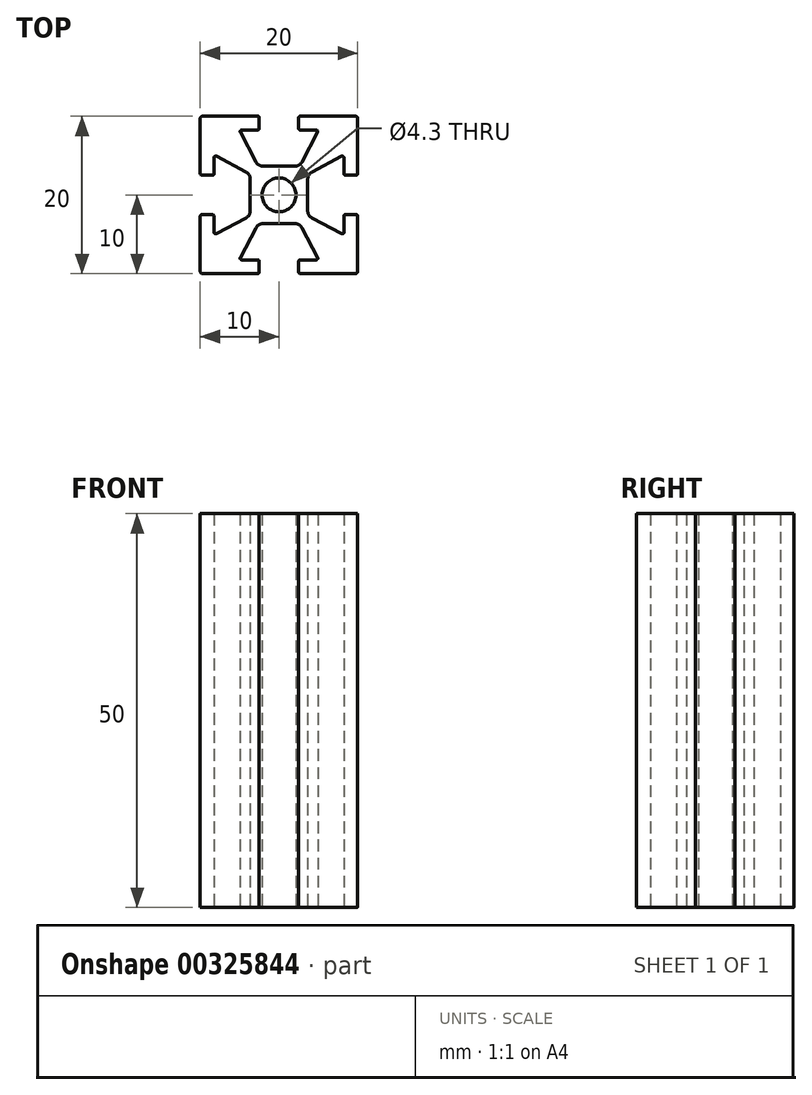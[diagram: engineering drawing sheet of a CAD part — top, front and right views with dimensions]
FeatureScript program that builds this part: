
annotation { "Feature Type Name" : "Feature", "Feature Type Description" : "" }
export const myFeature = defineFeature(function(context is Context, id is Id, definition is map)
    precondition{}
    {
        {
            var Q0;
            Q0=qCreatedBy(makeId("Top.planeOp"),FACE);
            var sketch = newSketch(context, id + "F0", { "sketchPlane" : qUnion([Q0])});
            skLineSegment(sketch, "E0", {"start": v(-9.7, 10) * mm, "end": v(-2.7, 10) * mm});
            skLineSegment(sketch, "E1", {"start": v(-2.5, 9.8) * mm, "end": v(-2.5, 8.45) * mm});
            skLineSegment(sketch, "E2", {"start": v(-2.7, 8.25) * mm, "end": v(-4.73, 8.25) * mm});
            skLineSegment(sketch, "E3", {"start": v(-4.9, 7.96) * mm, "end": v(-2.92, 4.18) * mm});
            skLineSegment(sketch, "E4", {"start": v(-2.03, 3.65) * mm, "end": v(0, 3.65) * mm});
            skLineSegment(sketch, "E5", {"start": v(0, 0) * mm, "end": v(-15.4, 15.4) * mm, "construction": true});
            skPoint(sketch, "E6.visualSharp", {"position": v(-5.06, 8.25) * mm});
            skArc(sketch, "E6.filletArc", {"start": v(-4.73, 8.25) * mm, "mid": v(-4.9, 8.15) * mm, "end": v(-4.9, 7.96) * mm});
            skPoint(sketch, "E7.visualSharp", {"position": v(-2.64, 3.65) * mm});
            skArc(sketch, "E7.filletArc", {"start": v(-2.92, 4.18) * mm, "mid": v(-2.55, 3.8) * mm, "end": v(-2.03, 3.65) * mm});
            skPoint(sketch, "E8.visualSharp", {"position": v(-2.5, 8.25) * mm});
            skArc(sketch, "E8.filletArc", {"start": v(-2.7, 8.25) * mm, "mid": v(-2.56, 8.3) * mm, "end": v(-2.5, 8.45) * mm});
            skPoint(sketch, "E9.visualSharp", {"position": v(-2.5, 10) * mm});
            skArc(sketch, "E9.filletArc", {"start": v(-2.5, 9.8) * mm, "mid": v(-2.56, 9.94) * mm, "end": v(-2.7, 10) * mm});
            skArc(sketch, "E10.MirrorCS", {"start": v(-8.25, 2.7) * mm, "mid": v(-8.3, 2.56) * mm, "end": v(-8.45, 2.5) * mm});
            skArc(sketch, "E11.MirrorCS", {"start": v(-4.18, 2.92) * mm, "mid": v(-3.8, 2.55) * mm, "end": v(-3.65, 2.03) * mm});
            skArc(sketch, "E12.MirrorCS", {"start": v(-9.8, 2.5) * mm, "mid": v(-9.94, 2.56) * mm, "end": v(-10, 2.7) * mm});
            skArc(sketch, "E13.MirrorCS", {"start": v(-8.25, 4.73) * mm, "mid": v(-8.15, 4.9) * mm, "end": v(-7.96, 4.9) * mm});
            skLineSegment(sketch, "E14.MirrorCS", {"start": v(-8.25, 2.7) * mm, "end": v(-8.25, 4.73) * mm});
            skLineSegment(sketch, "E15.MirrorCS", {"start": v(-9.8, 2.5) * mm, "end": v(-8.45, 2.5) * mm});
            skPoint(sketch, "E16.MirrorP", {"position": v(-10, 2.5) * mm});
            skPoint(sketch, "E17.MirrorP", {"position": v(-8.25, 5.06) * mm});
            skLineSegment(sketch, "E18.MirrorCS", {"start": v(-7.96, 4.9) * mm, "end": v(-4.18, 2.92) * mm});
            skPoint(sketch, "E19.MirrorP", {"position": v(-3.65, 2.64) * mm});
            skPoint(sketch, "E20.MirrorP", {"position": v(-8.25, 2.5) * mm});
            skLineSegment(sketch, "E21.MirrorCS", {"start": v(-10, 9.7) * mm, "end": v(-10, 2.7) * mm});
            skLineSegment(sketch, "E22.MirrorCS", {"start": v(-3.65, 2.03) * mm, "end": v(-3.65, 0) * mm});
            skPoint(sketch, "E23.visualSharp", {"position": v(-10, 10) * mm});
            skArc(sketch, "E23.filletArc", {"start": v(-9.7, 10) * mm, "mid": v(-9.91, 9.91) * mm, "end": v(-10, 9.7) * mm});
            skArc(sketch, "E24.MirrorCS", {"start": v(2.92, 4.18) * mm, "mid": v(2.55, 3.8) * mm, "end": v(2.03, 3.65) * mm});
            skArc(sketch, "E25.MirrorCS", {"start": v(4.18, 2.92) * mm, "mid": v(3.8, 2.55) * mm, "end": v(3.65, 2.03) * mm});
            skArc(sketch, "E26.MirrorCS", {"start": v(2.7, 8.25) * mm, "mid": v(2.56, 8.3) * mm, "end": v(2.5, 8.45) * mm});
            skArc(sketch, "E27.MirrorCS", {"start": v(8.25, 2.7) * mm, "mid": v(8.3, 2.56) * mm, "end": v(8.45, 2.5) * mm});
            skArc(sketch, "E28.MirrorCS", {"start": v(4.73, 8.25) * mm, "mid": v(4.9, 8.15) * mm, "end": v(4.9, 7.96) * mm});
            skArc(sketch, "E29.MirrorCS", {"start": v(9.7, 10) * mm, "mid": v(9.91, 9.91) * mm, "end": v(10, 9.7) * mm});
            skArc(sketch, "E30.MirrorCS", {"start": v(2.5, 9.8) * mm, "mid": v(2.56, 9.94) * mm, "end": v(2.7, 10) * mm});
            skArc(sketch, "E31.MirrorCS", {"start": v(9.8, 2.5) * mm, "mid": v(9.94, 2.56) * mm, "end": v(10, 2.7) * mm});
            skArc(sketch, "E32.MirrorCS", {"start": v(8.25, 4.73) * mm, "mid": v(8.15, 4.9) * mm, "end": v(7.96, 4.9) * mm});
            skLineSegment(sketch, "E33.MirrorCS", {"start": v(2.03, 3.65) * mm, "end": v(0, 3.65) * mm});
            skPoint(sketch, "E34.MirrorP", {"position": v(2.64, 3.65) * mm});
            skLineSegment(sketch, "E35.MirrorCS", {"start": v(3.65, 2.03) * mm, "end": v(3.65, 0) * mm});
            skLineSegment(sketch, "E36.MirrorCS", {"start": v(2.5, 9.8) * mm, "end": v(2.5, 8.45) * mm});
            skLineSegment(sketch, "E37.MirrorCS", {"start": v(8.25, 2.7) * mm, "end": v(8.25, 4.73) * mm});
            skPoint(sketch, "E38.MirrorP", {"position": v(8.25, 5.06) * mm});
            skLineSegment(sketch, "E39.MirrorCS", {"start": v(4.9, 7.96) * mm, "end": v(2.92, 4.18) * mm});
            skLineSegment(sketch, "E40.MirrorCS", {"start": v(7.96, 4.9) * mm, "end": v(4.18, 2.92) * mm});
            skPoint(sketch, "E41.MirrorP", {"position": v(8.25, 2.5) * mm});
            skPoint(sketch, "E42.MirrorP", {"position": v(5.06, 8.25) * mm});
            skPoint(sketch, "E43.MirrorP", {"position": v(10, 10) * mm});
            skPoint(sketch, "E44.MirrorP", {"position": v(10, 2.5) * mm});
            skLineSegment(sketch, "E45.MirrorCS", {"start": v(9.7, 10) * mm, "end": v(2.7, 10) * mm});
            skLineSegment(sketch, "E46.MirrorCS", {"start": v(9.8, 2.5) * mm, "end": v(8.45, 2.5) * mm});
            skPoint(sketch, "E47.MirrorP", {"position": v(2.5, 8.25) * mm});
            skPoint(sketch, "E48.MirrorP", {"position": v(2.5, 10) * mm});
            skLineSegment(sketch, "E49.MirrorCS", {"start": v(10, 9.7) * mm, "end": v(10, 2.7) * mm});
            skLineSegment(sketch, "E50.MirrorCS", {"start": v(2.7, 8.25) * mm, "end": v(4.73, 8.25) * mm});
            skPoint(sketch, "E51.MirrorP", {"position": v(3.65, 2.64) * mm});
            skArc(sketch, "E52.MirrorCS", {"start": v(-9.7, -10) * mm, "mid": v(-9.91, -9.91) * mm, "end": v(-10, -9.7) * mm});
            skArc(sketch, "E53.MirrorCS", {"start": v(-2.92, -4.18) * mm, "mid": v(-2.55, -3.8) * mm, "end": v(-2.03, -3.65) * mm});
            skArc(sketch, "E54.MirrorCS", {"start": v(-4.18, -2.92) * mm, "mid": v(-3.8, -2.55) * mm, "end": v(-3.65, -2.03) * mm});
            skArc(sketch, "E55.MirrorCS", {"start": v(2.92, -4.18) * mm, "mid": v(2.55, -3.8) * mm, "end": v(2.03, -3.65) * mm});
            skArc(sketch, "E56.MirrorCS", {"start": v(4.18, -2.92) * mm, "mid": v(3.8, -2.55) * mm, "end": v(3.65, -2.03) * mm});
            skArc(sketch, "E57.MirrorCS", {"start": v(2.7, -8.25) * mm, "mid": v(2.56, -8.3) * mm, "end": v(2.5, -8.45) * mm});
            skArc(sketch, "E58.MirrorCS", {"start": v(9.7, -10) * mm, "mid": v(9.91, -9.91) * mm, "end": v(10, -9.7) * mm});
            skArc(sketch, "E59.MirrorCS", {"start": v(-4.73, -8.25) * mm, "mid": v(-4.9, -8.15) * mm, "end": v(-4.9, -7.96) * mm});
            skArc(sketch, "E60.MirrorCS", {"start": v(8.25, -2.7) * mm, "mid": v(8.3, -2.56) * mm, "end": v(8.45, -2.5) * mm});
            skArc(sketch, "E61.MirrorCS", {"start": v(2.5, -9.8) * mm, "mid": v(2.56, -9.94) * mm, "end": v(2.7, -10) * mm});
            skArc(sketch, "E62.MirrorCS", {"start": v(-9.8, -2.5) * mm, "mid": v(-9.94, -2.56) * mm, "end": v(-10, -2.7) * mm});
            skArc(sketch, "E63.MirrorCS", {"start": v(-8.25, -4.73) * mm, "mid": v(-8.15, -4.9) * mm, "end": v(-7.96, -4.9) * mm});
            skArc(sketch, "E64.MirrorCS", {"start": v(-2.7, -8.25) * mm, "mid": v(-2.56, -8.3) * mm, "end": v(-2.5, -8.45) * mm});
            skArc(sketch, "E65.MirrorCS", {"start": v(8.25, -4.73) * mm, "mid": v(8.15, -4.9) * mm, "end": v(7.96, -4.9) * mm});
            skArc(sketch, "E66.MirrorCS", {"start": v(4.73, -8.25) * mm, "mid": v(4.9, -8.15) * mm, "end": v(4.9, -7.96) * mm});
            skArc(sketch, "E67.MirrorCS", {"start": v(-8.25, -2.7) * mm, "mid": v(-8.3, -2.56) * mm, "end": v(-8.45, -2.5) * mm});
            skArc(sketch, "E68.MirrorCS", {"start": v(-2.5, -9.8) * mm, "mid": v(-2.56, -9.94) * mm, "end": v(-2.7, -10) * mm});
            skArc(sketch, "E69.MirrorCS", {"start": v(9.8, -2.5) * mm, "mid": v(9.94, -2.56) * mm, "end": v(10, -2.7) * mm});
            skLineSegment(sketch, "E70.MirrorCS", {"start": v(7.96, -4.9) * mm, "end": v(4.18, -2.92) * mm});
            skPoint(sketch, "E71.MirrorP", {"position": v(2.64, -3.65) * mm});
            skLineSegment(sketch, "E72.MirrorCS", {"start": v(-3.65, -2.03) * mm, "end": v(-3.65, 0) * mm});
            skLineSegment(sketch, "E73.MirrorCS", {"start": v(2.7, -8.25) * mm, "end": v(4.73, -8.25) * mm});
            skLineSegment(sketch, "E74.MirrorCS", {"start": v(2.5, -9.8) * mm, "end": v(2.5, -8.45) * mm});
            skPoint(sketch, "E75.MirrorP", {"position": v(-2.5, -8.25) * mm});
            skPoint(sketch, "E76.MirrorP", {"position": v(2.5, -10) * mm});
            skPoint(sketch, "E77.MirrorP", {"position": v(-8.25, -2.5) * mm});
            skPoint(sketch, "E78.MirrorP", {"position": v(8.25, -2.5) * mm});
            skLineSegment(sketch, "E79.MirrorCS", {"start": v(9.8, -2.5) * mm, "end": v(8.45, -2.5) * mm});
            skPoint(sketch, "E80.MirrorP", {"position": v(10, -10) * mm});
            skLineSegment(sketch, "E81.MirrorCS", {"start": v(-9.7, -10) * mm, "end": v(-2.7, -10) * mm});
            skPoint(sketch, "E82.MirrorP", {"position": v(10, -2.5) * mm});
            skLineSegment(sketch, "E83.MirrorCS", {"start": v(-7.96, -4.9) * mm, "end": v(-4.18, -2.92) * mm});
            skLineSegment(sketch, "E84.MirrorCS", {"start": v(-2.7, -8.25) * mm, "end": v(-4.73, -8.25) * mm});
            skLineSegment(sketch, "E85.MirrorCS", {"start": v(-2.03, -3.65) * mm, "end": v(0, -3.65) * mm});
            skPoint(sketch, "E86.MirrorP", {"position": v(-10, -10) * mm});
            skLineSegment(sketch, "E87.MirrorCS", {"start": v(-9.8, -2.5) * mm, "end": v(-8.45, -2.5) * mm});
            skPoint(sketch, "E88.MirrorP", {"position": v(-5.06, -8.25) * mm});
            skLineSegment(sketch, "E89.MirrorCS", {"start": v(-2.5, -9.8) * mm, "end": v(-2.5, -8.45) * mm});
            skPoint(sketch, "E90.MirrorP", {"position": v(-2.64, -3.65) * mm});
            skLineSegment(sketch, "E91.MirrorCS", {"start": v(9.7, -10) * mm, "end": v(2.7, -10) * mm});
            skPoint(sketch, "E92.MirrorP", {"position": v(3.65, -2.64) * mm});
            skLineSegment(sketch, "E93.MirrorCS", {"start": v(-4.9, -7.96) * mm, "end": v(-2.92, -4.18) * mm});
            skPoint(sketch, "E94.MirrorP", {"position": v(-10, -2.5) * mm});
            skPoint(sketch, "E95.MirrorP", {"position": v(5.06, -8.25) * mm});
            skPoint(sketch, "E96.MirrorP", {"position": v(-3.65, -2.64) * mm});
            skLineSegment(sketch, "E97.MirrorCS", {"start": v(-8.25, -2.7) * mm, "end": v(-8.25, -4.73) * mm});
            skLineSegment(sketch, "E98.MirrorCS", {"start": v(2.03, -3.65) * mm, "end": v(0, -3.65) * mm});
            skPoint(sketch, "E99.MirrorP", {"position": v(2.5, -8.25) * mm});
            skLineSegment(sketch, "E100.MirrorCS", {"start": v(8.25, -2.7) * mm, "end": v(8.25, -4.73) * mm});
            skPoint(sketch, "E101.MirrorP", {"position": v(8.25, -5.06) * mm});
            skLineSegment(sketch, "E102.MirrorCS", {"start": v(4.9, -7.96) * mm, "end": v(2.92, -4.18) * mm});
            skLineSegment(sketch, "E103.MirrorCS", {"start": v(3.65, -2.03) * mm, "end": v(3.65, 0) * mm});
            skPoint(sketch, "E104.MirrorP", {"position": v(-2.5, -10) * mm});
            skLineSegment(sketch, "E105.MirrorCS", {"start": v(-10, -9.7) * mm, "end": v(-10, -2.7) * mm});
            skLineSegment(sketch, "E106.MirrorCS", {"start": v(10, -9.7) * mm, "end": v(10, -2.7) * mm});
            skPoint(sketch, "E107.MirrorP", {"position": v(-8.25, -5.06) * mm});
            skCircle(sketch, "E108", {"center": v(0, 0) * mm, "radius": 2.15 * mm});
            skSolve(sketch);
        }
        {
            var Q0;
            Q0=makeQuery(id+"F0.imprint","IMPRINT",FACE,{"disambiguationData":[TD([[makeQuery(id+"F0.imprint","IMPRINT",EDGE,{"derivedFrom":sQuery(id+"F0.wireOp",EDGE,"E0")}),-1.0]])]});
            extrude(context, id + "F1", {"entities" : qUnion([Q0]), "depth" : 50 * mm});
        }
    });
